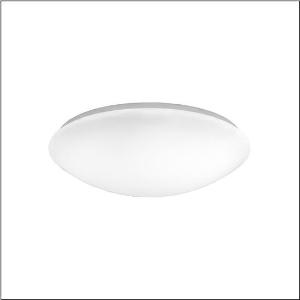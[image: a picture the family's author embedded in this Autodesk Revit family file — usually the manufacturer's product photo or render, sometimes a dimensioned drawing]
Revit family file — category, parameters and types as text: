
# Revit family: round_31_b_5pja232001a
name_source: partatom
category: Lighting Fixtures
units: mm (PartAtom-declared; Revit-internal decimal feet)

## family parameters
Cut with Voids When Loaded = No
Host = Face
Light Source = No
Part Type = Normal
Room Calculation Point = No
Round Connector Dimension = Use Diameter
Shared = No

## types (1)
- --- (1 x LED, 4900 lm, 39 W, 4000K)
    Apparent Load = 39 VA
    CIE Flux Codes = 42 71 89 88 100
    Color Rendering = 80
    Color Temperature = 4000K
    Default Elevation = 1800 mm
    Description = Round 31 B, wall and ceiling luminaire, primary optical cover: enclosure, of PMMA, light emission: direct distribution, primary light characteristic: symmetric, installation type: surface-mounted, LED, rated luminous flux: 4.900lm, luminous efficacy: 126lm/W, light colour: 840, colour temperature: 4000K, with terminal, 3+2-pole, max. 2.5mm², mains connection: 230V, AC, 50/60Hz, rated input power: 39W, luminaire housing, round, of steel, white, diameter: 464mm, height: 120mm, protection rating (complete): IP40, insulation class (complete): insulation class I (protective earthing), certification: CE, impact resistance: IK02, packaging unit: 1 piece
    Height = 120 mm
    Lamp = 1 x LED
    Lamp Light Flux = 4900 lm
    Lamp Power = 39 W
    Lamp count = 1
    Length = 464 mm
    Luminous efficacy = 126 lm/W
    Manufacturer = Siteco
    ModVariant = No
    Model = 5PJA232001A
    Mounting Place = Ceiling
    Mounting Type = Surface mounted
    Number of Poles = 1
    OnlyDefault = Yes
    Power Factor = 1
    Product Name = Round 31 B
    Product group = wall and ceiling luminaire
    ProductGroupID = 302
    Protection Class = Protection class I
    Protection Degree = IP 40
    RLX_Detail_Level = 1
    RLX_Emergency_Light_Flux = 0 lm
    RLX_Emergency_Type = 0
    RLX_Emergency_Type_DB = No
    RlxData = <blob elided: 13753 chars, md5=063128f2>
    Socket = socket
    Standby Power = 0 W
    System Light Flux = 4900 lm
    System Power = 39 W
    Type Comments = factory setting: luminous flux: 100 % | (ON | ON | ON) | 1050 mA
    Type Image = l_1258313.jpg
    URL = http://relux.com
    VarID = @adj_032335
    Voltage = 0 V
    Weight = 0.00 kg
    Width = 0 mm  [stored 0 ft]

note: [stored X ft] marks values corroborated as IEEE doubles in the binary element streams (Revit-internal decimal feet)

## geometry (parser evidence)
native form markers: Sweep x12
no freeform markers — native parametric forms only
